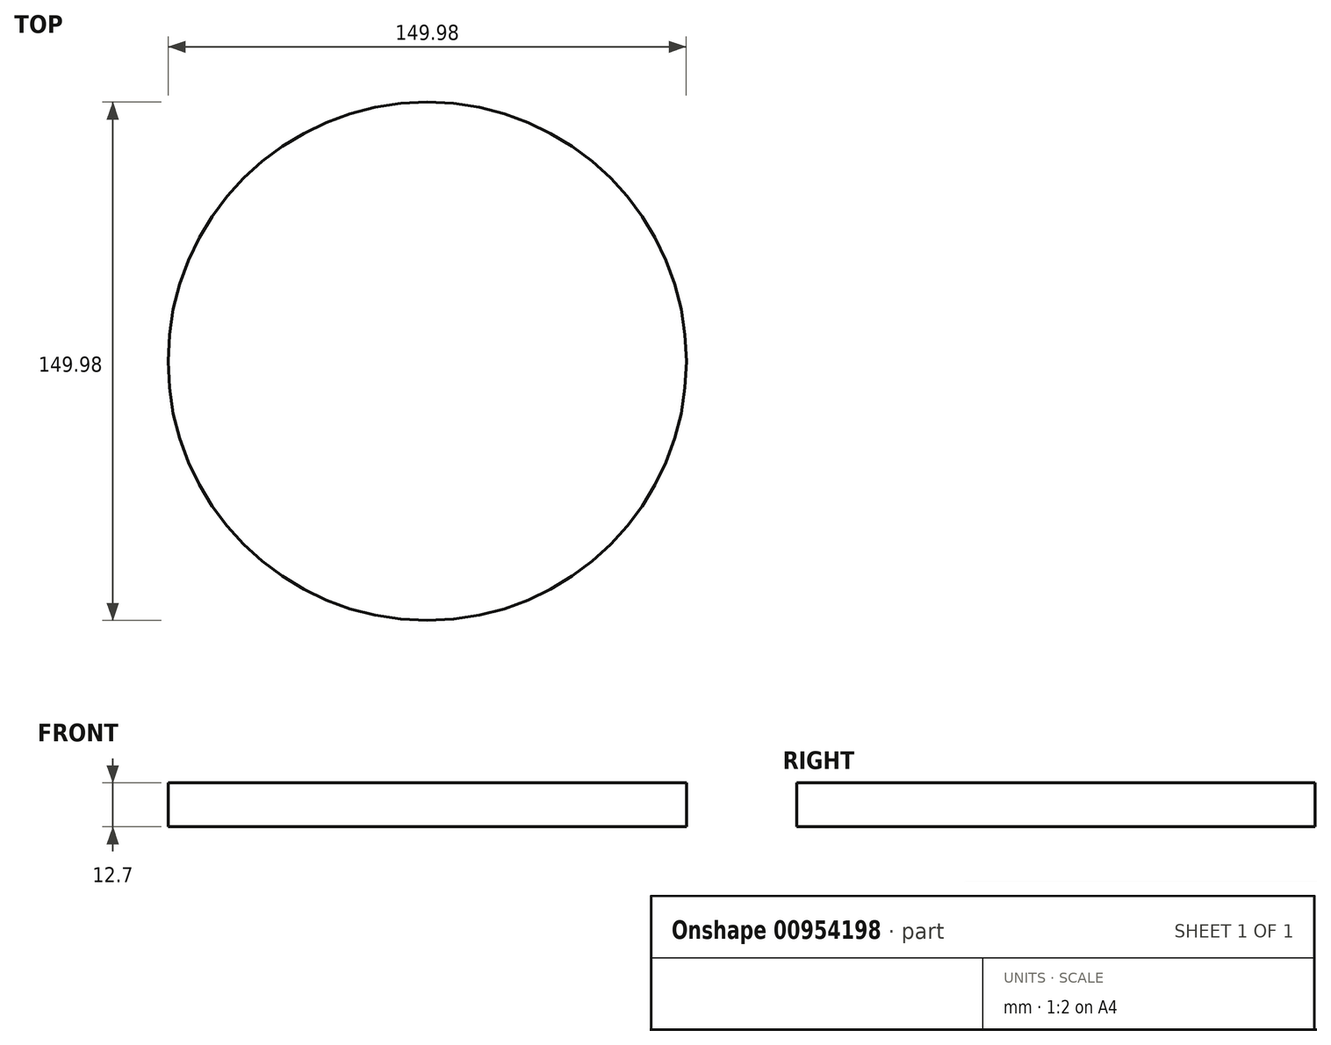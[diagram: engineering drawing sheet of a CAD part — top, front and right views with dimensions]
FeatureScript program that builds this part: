
annotation { "Feature Type Name" : "Feature", "Feature Type Description" : "" }
export const myFeature = defineFeature(function(context is Context, id is Id, definition is map)
    precondition{}
    {
        {
            var Q0;
            Q0=qCreatedBy(makeId("Top.planeOp"),FACE);
            var sketch = newSketch(context, id + "F0", { "sketchPlane" : qUnion([Q0])});
            skCircle(sketch, "E0", {"center": v(0, 0) * mm, "radius": 75 * mm});
            skSolve(sketch);
        }
        {
            var Q0;
            Q0 = qSketchRegion(id + "F0", true);
            extrude(context, id + "F1", {"entities" : qUnion([Q0]), "depth" : 12.7 * mm, "offsetDistance" : 25.4 * mm});
        }
    });
